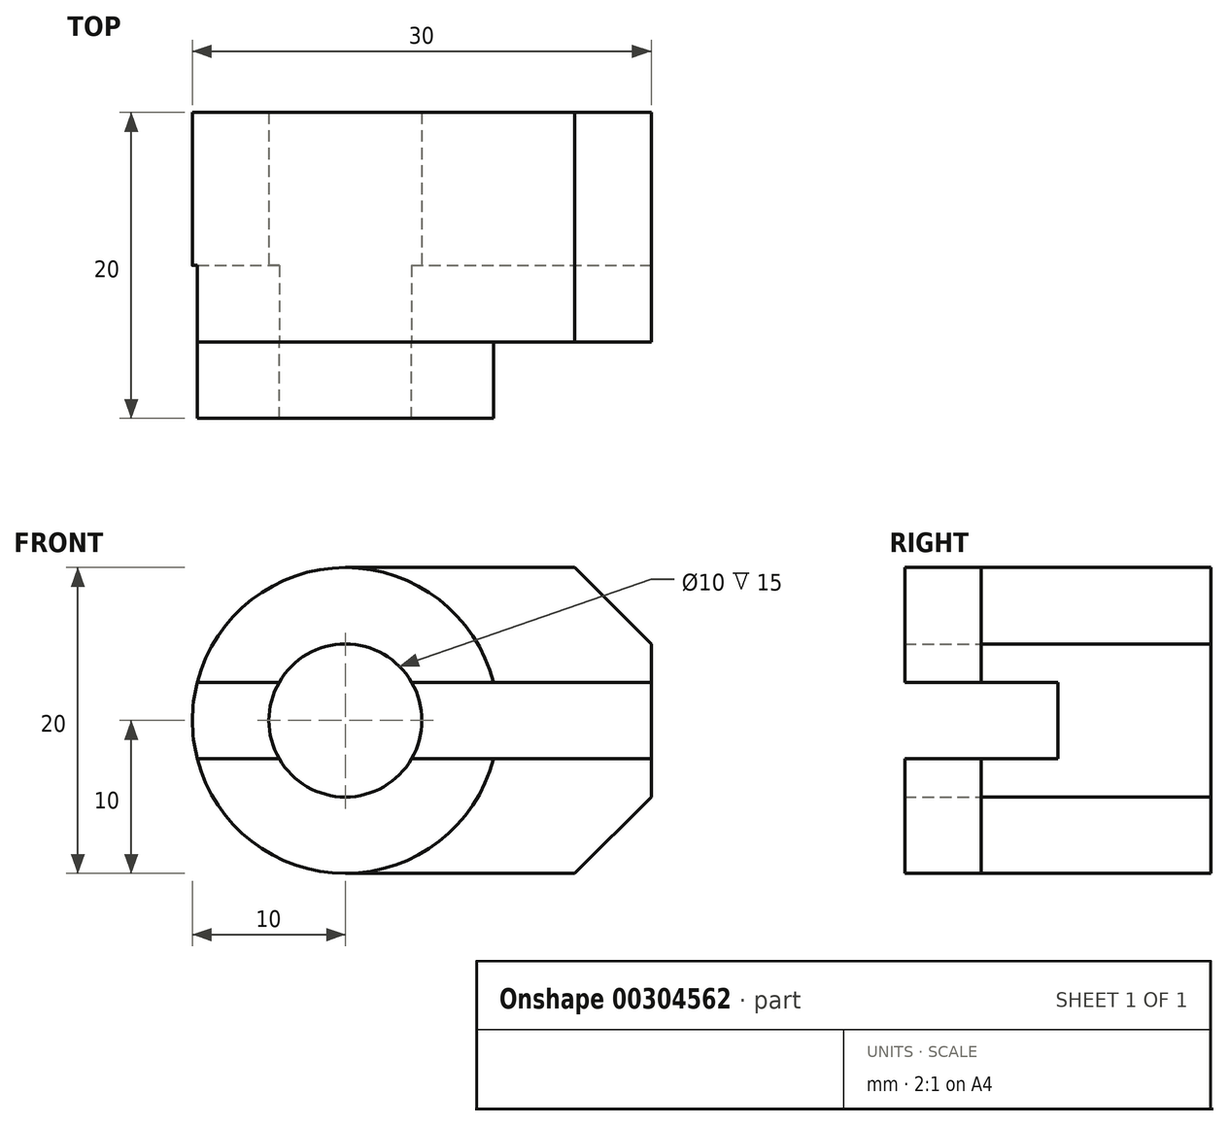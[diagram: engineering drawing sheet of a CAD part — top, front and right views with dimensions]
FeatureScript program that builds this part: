
annotation { "Feature Type Name" : "Feature", "Feature Type Description" : "" }
export const myFeature = defineFeature(function(context is Context, id is Id, definition is map)
    precondition{}
    {
        {
            var Q0;
            Q0=qCreatedBy(makeId("Front.planeOp"),FACE);
            var sketch = newSketch(context, id + "F0", { "sketchPlane" : qUnion([Q0])});
            skCircle(sketch, "E0", {"center": v(0, 0) * mm, "radius": 5 * mm});
            skArc(sketch, "E1", {"start": v(0, -10) * mm, "mid": v(-10, 0) * mm, "end": v(0, 10) * mm});
            skLineSegment(sketch, "E2", {"start": v(0, 10) * mm, "end": v(15, 10) * mm});
            skLineSegment(sketch, "E3", {"start": v(0, -10) * mm, "end": v(15, -10) * mm});
            skArc(sketch, "E4", {"start": v(9.68, 2.5) * mm, "mid": v(-10, 0) * mm, "end": v(9.68, -2.5) * mm});
            skLineSegment(sketch, "E5", {"start": v(-14.45, 0) * mm, "end": v(28.13, 0) * mm, "construction": true});
            skLineSegment(sketch, "E6", {"start": v(-9.68, 2.5) * mm, "end": v(-4.33, 2.5) * mm});
            skLineSegment(sketch, "E7", {"start": v(-9.68, -2.5) * mm, "end": v(-4.33, -2.5) * mm});
            skLineSegment(sketch, "E8", {"start": v(15, 10) * mm, "end": v(20, 5) * mm});
            skLineSegment(sketch, "E9", {"start": v(20, 5) * mm, "end": v(20, -5) * mm});
            skLineSegment(sketch, "E10", {"start": v(20, -5) * mm, "end": v(15, -10) * mm});
            skLineSegment(sketch, "E11", {"start": v(4.33, 2.5) * mm, "end": v(20, 2.5) * mm});
            skLineSegment(sketch, "E12", {"start": v(4.33, -2.5) * mm, "end": v(20, -2.5) * mm});
            skSolve(sketch);
        }
        {
            var Q0;
            {var subQ2=sQuery(id+"F0.wireOp",EDGE,"E6");Q0=makeQuery(id+"F0.imprint","IMPRINT",FACE,{"disambiguationData":[TD([[makeQuery(id+"F0.imprint","IMPRINT",EDGE,{"derivedFrom":subQ2}),1.0]])]});}
            var Q1;
            {var subQ4=sQuery(id+"F0.wireOp",EDGE,"E7");Q1=makeQuery(id+"F0.imprint","IMPRINT",FACE,{"disambiguationData":[TD([[makeQuery(id+"F0.imprint","IMPRINT",EDGE,{"derivedFrom":subQ4}),-1.0]])]});}
            extrude(context, id + "F1", {"entities" : qUnion([Q0, Q1]), "depth" : 5 * mm});
        }
        {
            var Q0;
            {var subQ2=sQuery(id+"F0.wireOp",EDGE,"E2");Q0=makeQuery(id+"F0.imprint","IMPRINT",FACE,{"disambiguationData":[TD([[makeQuery(id+"F0.imprint","IMPRINT",EDGE,{"derivedFrom":subQ2}),-1.0]])]});}
            var Q1;
            {var subQ0=sQuery(id+"F0.wireOp",EDGE,"E11");var subQ7=sQuery(id+"F0.wireOp",EDGE,"E0");var subQ8=makeQuery(id+"F0.imprint","INTERSECT",VERTEX,{"derivedFrom":[subQ7,subQ0]});Q1=makeQuery(id+"F0.imprint","IMPRINT",FACE,{"disambiguationData":[TD([[makeQuery(id+"F0.imprint","IMPRINT",EDGE,{"disambiguationData":[TD([[subQ8,1.0]])],"derivedFrom":subQ7}),-1.0]])]});}
            var Q2;
            {var subQ0=sQuery(id+"F0.wireOp",EDGE,"E6");Q2=makeQuery(id+"F0.imprint","IMPRINT",FACE,{"disambiguationData":[TD([[makeQuery(id+"F0.imprint","IMPRINT",EDGE,{"derivedFrom":subQ0}),-1.0]])]});}
            var Q3;
            {var subQ4=sQuery(id+"F0.wireOp",EDGE,"E3");Q3=makeQuery(id+"F0.imprint","IMPRINT",FACE,{"disambiguationData":[TD([[makeQuery(id+"F0.imprint","IMPRINT",EDGE,{"derivedFrom":subQ4}),1.0]])]});}
            var Q4;
            {var subQ2=sQuery(id+"F0.wireOp",EDGE,"E6");Q4=makeQuery(id+"F0.imprint","IMPRINT",FACE,{"disambiguationData":[TD([[makeQuery(id+"F0.imprint","IMPRINT",EDGE,{"derivedFrom":subQ2}),1.0]])]});}
            var Q5;
            {var subQ4=sQuery(id+"F0.wireOp",EDGE,"E7");Q5=makeQuery(id+"F0.imprint","IMPRINT",FACE,{"disambiguationData":[TD([[makeQuery(id+"F0.imprint","IMPRINT",EDGE,{"derivedFrom":subQ4}),-1.0]])]});}
            extrude(context, id + "F2", {"entities" : qUnion([Q0, Q1, Q2, Q3, Q4, Q5]), "oppositeDirection" : true, "depth" : 15 * mm});
        }
        {
            var Q0;
            {var subQ0=sQuery(id+"F0.wireOp",EDGE,"E11");var subQ7=sQuery(id+"F0.wireOp",EDGE,"E0");var subQ8=makeQuery(id+"F0.imprint","INTERSECT",VERTEX,{"derivedFrom":[subQ7,subQ0]});Q0=makeQuery(id+"F0.imprint","IMPRINT",FACE,{"disambiguationData":[TD([[makeQuery(id+"F0.imprint","IMPRINT",EDGE,{"disambiguationData":[TD([[subQ8,1.0]])],"derivedFrom":subQ7}),-1.0]])]});}
            var Q1;
            {var subQ0=sQuery(id+"F0.wireOp",EDGE,"E6");Q1=makeQuery(id+"F0.imprint","IMPRINT",FACE,{"disambiguationData":[TD([[makeQuery(id+"F0.imprint","IMPRINT",EDGE,{"derivedFrom":subQ0}),-1.0]])]});}
            extrude(context, id + "F3", {"entities" : qUnion([Q0, Q1]), "operationType" : NewBodyOperationType.REMOVE, "oppositeDirection" : true, "depth" : 5 * mm});
        }
    });
